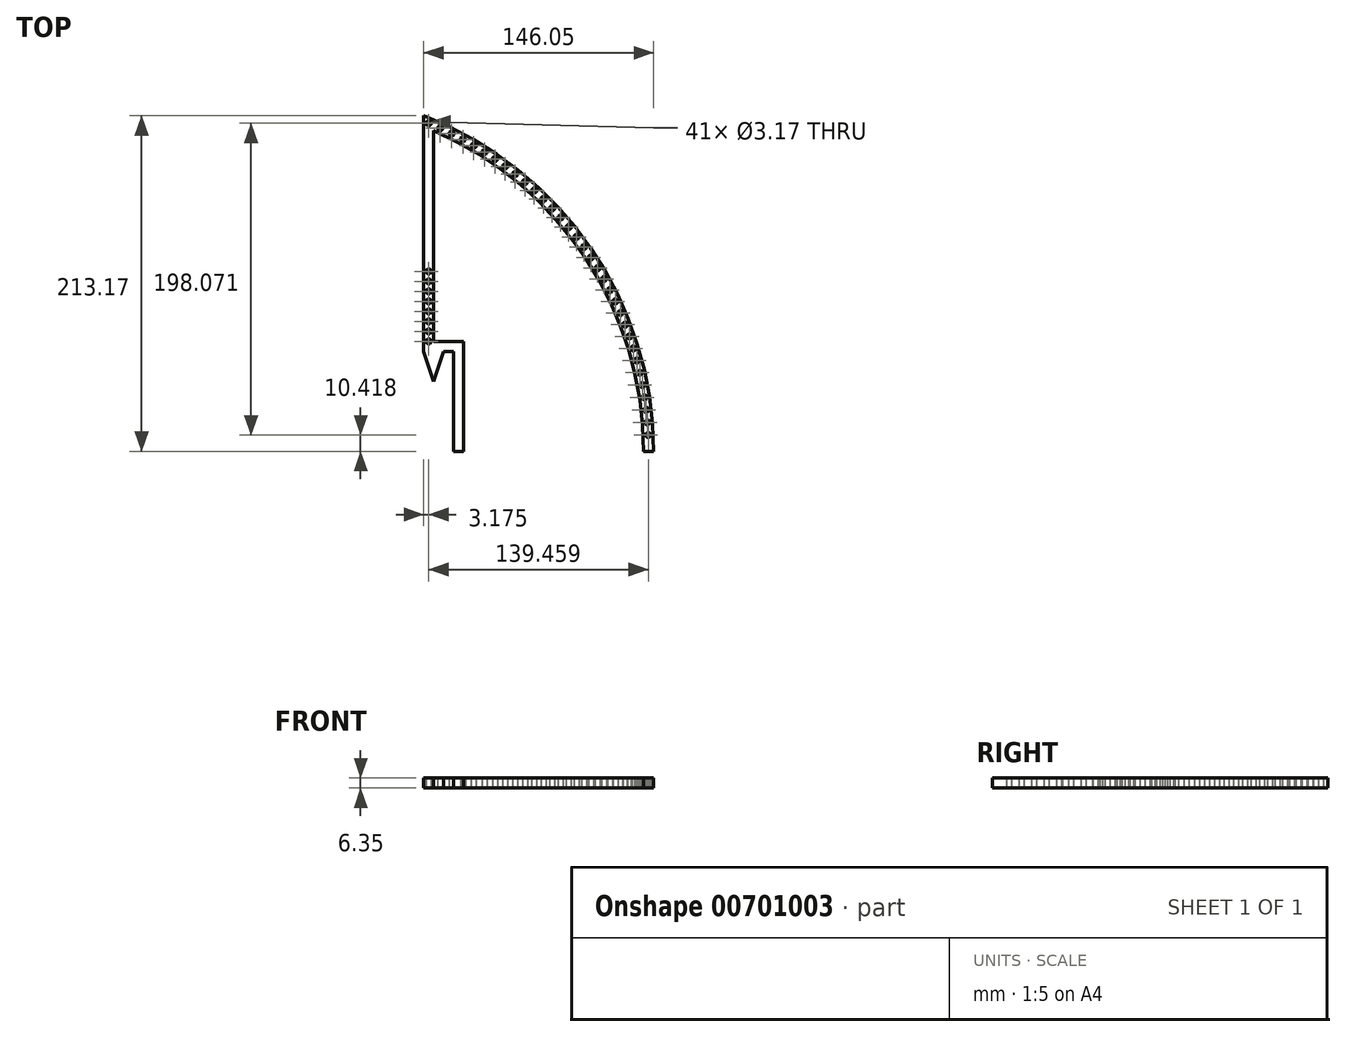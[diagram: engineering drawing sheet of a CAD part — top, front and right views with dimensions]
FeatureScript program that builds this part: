
annotation { "Feature Type Name" : "Feature", "Feature Type Description" : "" }
export const myFeature = defineFeature(function(context is Context, id is Id, definition is map)
    precondition{}
    {
        {
            var Q0;
            Q0=qCreatedBy(makeId("Top.planeOp"),FACE);
            var sketch = newSketch(context, id + "F0", { "sketchPlane" : qUnion([Q0])});
            skLineSegment(sketch, "E0", {"start": v(0, 0) * mm, "end": v(-82.55, 0) * mm, "construction": true});
            skCircle(sketch, "E1", {"center": v(-82.55, 0) * mm, "radius": 254 * mm, "construction": true});
            skLineSegment(sketch, "E2", {"start": v(0, 0) * mm, "end": v(0, 63.5) * mm, "construction": true});
            skLineSegment(sketch, "E3", {"start": v(0, 0) * mm, "end": v(19.05, 0) * mm, "construction": true});
            skLineSegment(sketch, "E4", {"start": v(19.05, 0) * mm, "end": v(19.05, 63.5) * mm});
            skLineSegment(sketch, "E5", {"start": v(19.05, 63.5) * mm, "end": v(12.7, 63.5) * mm});
            skLineSegment(sketch, "E6", {"start": v(0, 63.5) * mm, "end": v(12.7, 63.5) * mm, "construction": true});
            skLineSegment(sketch, "E7", {"start": v(6.35, 63.5) * mm, "end": v(6.35, 44.45) * mm, "construction": true});
            skLineSegment(sketch, "E8", {"start": v(0, 63.5) * mm, "end": v(6.35, 44.45) * mm});
            skLineSegment(sketch, "E9", {"start": v(12.7, 63.5) * mm, "end": v(6.35, 44.45) * mm});
            skCircle(sketch, "E10", {"center": v(-82.55, 0) * mm, "radius": 228.6 * mm, "construction": true});
            skLineSegment(sketch, "E11", {"start": v(0, 63.5) * mm, "end": v(0, 213.17) * mm});
            skArc(sketch, "E12", {"start": v(0, 213.17) * mm, "mid": v(106.04, 129.2) * mm, "end": v(146.05, 0) * mm});
            skArc(sketch, "E13.0", {"start": v(6.35, 203.7) * mm, "mid": v(103.4, 121.73) * mm, "end": v(139.7, 0) * mm});
            skLineSegment(sketch, "E13.1", {"start": v(25.4, 0) * mm, "end": v(25.4, 69.85) * mm});
            skLineSegment(sketch, "E13.2", {"start": v(25.4, 69.85) * mm, "end": v(12.7, 69.85) * mm});
            skLineSegment(sketch, "E13.3", {"start": v(6.35, 69.85) * mm, "end": v(12.7, 69.85) * mm});
            skLineSegment(sketch, "E13.4", {"start": v(6.35, 69.85) * mm, "end": v(6.35, 203.7) * mm});
            skLineSegment(sketch, "E14", {"start": v(19.05, 0) * mm, "end": v(25.4, 0) * mm});
            skLineSegment(sketch, "E15", {"start": v(139.7, 0) * mm, "end": v(146.05, 0) * mm});
            skLineSegment(sketch, "E16", {"start": v(6.35, 203.7) * mm, "end": v(0, 203.7) * mm, "construction": true});
            skLineSegment(sketch, "E17", {"start": v(3.17, 203.7) * mm, "end": v(3.17, 69.85) * mm, "construction": true});
            skCircle(sketch, "E18", {"center": v(3.17, 69.85) * mm, "radius": 1.59 * mm});
            skCircle(sketch, "E19.0.1.0", {"center": v(3.17, 76.2) * mm, "radius": 1.59 * mm});
            skCircle(sketch, "E19.0.2.0", {"center": v(3.17, 82.55) * mm, "radius": 1.59 * mm});
            skCircle(sketch, "E19.0.3.0", {"center": v(3.17, 88.9) * mm, "radius": 1.59 * mm});
            skCircle(sketch, "E19.0.4.0", {"center": v(3.17, 95.25) * mm, "radius": 1.59 * mm});
            skCircle(sketch, "E19.0.5.0", {"center": v(3.17, 101.6) * mm, "radius": 1.59 * mm});
            skLineSegment(sketch, "E19.direction1", {"start": v(3.17, 69.85) * mm, "end": v(28.57, 69.85) * mm, "construction": true});
            skLineSegment(sketch, "E19.direction2", {"start": v(3.17, 69.85) * mm, "end": v(3.17, 76.2) * mm, "construction": true});
            skCircle(sketch, "E20.0.0.6", {"center": v(3.17, 107.95) * mm, "radius": 1.59 * mm});
            skCircle(sketch, "E20.0.0.7", {"center": v(3.17, 114.3) * mm, "radius": 1.59 * mm});
            skCircle(sketch, "E21", {"center": v(-82.55, 0) * mm, "radius": 225.43 * mm, "construction": true});
            skCircle(sketch, "E22", {"center": v(3.17, 208.49) * mm, "radius": 1.59 * mm});
            skCircle(sketch, "E23.1.0", {"center": v(10.51, 205.32) * mm, "radius": 1.59 * mm});
            skCircle(sketch, "E23.2.0", {"center": v(17.73, 201.9) * mm, "radius": 1.59 * mm});
            skCircle(sketch, "E23.3.0", {"center": v(24.82, 198.21) * mm, "radius": 1.59 * mm});
            skCircle(sketch, "E23.4.0", {"center": v(31.78, 194.28) * mm, "radius": 1.59 * mm});
            skCircle(sketch, "E23.5.0", {"center": v(38.6, 190.1) * mm, "radius": 1.59 * mm});
            skCircle(sketch, "E23.6.0", {"center": v(45.26, 185.7) * mm, "radius": 1.59 * mm});
            skCircle(sketch, "E23.7.0", {"center": v(51.76, 181.05) * mm, "radius": 1.59 * mm});
            skCircle(sketch, "E23.8.0", {"center": v(58.1, 176.17) * mm, "radius": 1.59 * mm});
            skCircle(sketch, "E23.9.0", {"center": v(64.25, 171.08) * mm, "radius": 1.59 * mm});
            skCircle(sketch, "E23.10.0", {"center": v(70.22, 165.77) * mm, "radius": 1.59 * mm});
            skCircle(sketch, "E23.11.0", {"center": v(76, 160.25) * mm, "radius": 1.59 * mm});
            skCircle(sketch, "E23.12.0", {"center": v(81.58, 154.53) * mm, "radius": 1.59 * mm});
            skCircle(sketch, "E23.13.0", {"center": v(86.95, 148.61) * mm, "radius": 1.59 * mm});
            skCircle(sketch, "E23.14.0", {"center": v(92.11, 142.5) * mm, "radius": 1.59 * mm});
            skCircle(sketch, "E23.15.0", {"center": v(97.06, 136.23) * mm, "radius": 1.59 * mm});
            skCircle(sketch, "E23.16.0", {"center": v(101.77, 129.78) * mm, "radius": 1.59 * mm});
            skCircle(sketch, "E23.17.0", {"center": v(106.25, 123.16) * mm, "radius": 1.59 * mm});
            skCircle(sketch, "E23.18.0", {"center": v(110.5, 116.4) * mm, "radius": 1.59 * mm});
            skCircle(sketch, "E23.19.0", {"center": v(114.5, 109.48) * mm, "radius": 1.59 * mm});
            skCircle(sketch, "E23.20.0", {"center": v(118.26, 102.42) * mm, "radius": 1.59 * mm});
            skCircle(sketch, "E23.21.0", {"center": v(121.77, 95.24) * mm, "radius": 1.59 * mm});
            skCircle(sketch, "E23.22.0", {"center": v(125.01, 87.94) * mm, "radius": 1.59 * mm});
            skCircle(sketch, "E23.23.0", {"center": v(128, 80.53) * mm, "radius": 1.59 * mm});
            skCircle(sketch, "E23.24.0", {"center": v(130.72, 73.01) * mm, "radius": 1.59 * mm});
            skCircle(sketch, "E23.25.0", {"center": v(133.18, 65.4) * mm, "radius": 1.59 * mm});
            skCircle(sketch, "E23.26.0", {"center": v(135.36, 57.72) * mm, "radius": 1.59 * mm});
            skCircle(sketch, "E23.27.0", {"center": v(137.27, 49.96) * mm, "radius": 1.59 * mm});
            skCircle(sketch, "E23.28.0", {"center": v(138.9, 42.14) * mm, "radius": 1.59 * mm});
            skCircle(sketch, "E23.29.0", {"center": v(140.26, 34.26) * mm, "radius": 1.59 * mm});
            skCircle(sketch, "E23.30.0", {"center": v(141.33, 26.34) * mm, "radius": 1.59 * mm});
            skCircle(sketch, "E23.31.0", {"center": v(142.12, 18.4) * mm, "radius": 1.59 * mm});
            skCircle(sketch, "E23.32.0", {"center": v(142.63, 10.42) * mm, "radius": 1.59 * mm});
            skLineSegment(sketch, "E23.anchor1", {"start": v(-82.55, 0) * mm, "end": v(3.17, 208.49) * mm, "construction": true});
            skLineSegment(sketch, "E23.anchor2", {"start": v(-82.55, 0) * mm, "end": v(142.63, 10.42) * mm, "construction": true});
            skLineSegment(sketch, "E24", {"start": v(0, 213.17) * mm, "end": v(-165.1, 213.17) * mm, "construction": true});
            skArc(sketch, "E25", {"start": v(-165.1, 213.17) * mm, "mid": v(-82.55, 228.6) * mm, "end": v(0, 213.17) * mm});
            skLineSegment(sketch, "E26", {"start": v(-165.1, 213.17) * mm, "end": v(-165.1, 175.07) * mm});
            skLineSegment(sketch, "E27", {"start": v(-165.1, 175.07) * mm, "end": v(0, 175.07) * mm});
            skLineSegment(sketch, "E28", {"start": v(-82.55, 175.07) * mm, "end": v(-82.55, 228.6) * mm, "construction": true});
            skLineSegment(sketch, "E29", {"start": v(-82.55, 175.07) * mm, "end": v(-82.55, 181.42) * mm, "construction": true});
            skSolve(sketch);
        }
        {
            var Q0;
            Q0=makeQuery(id+"F0.imprint","IMPRINT",FACE,{"disambiguationData":[TD([[makeQuery(id+"F0.imprint","IMPRINT",EDGE,{"derivedFrom":sQuery(id+"F0.wireOp",EDGE,"E4")}),-1.0]])]});
            extrude(context, id + "F1", {"entities" : qUnion([Q0]), "depth" : 6.35 * mm, "offsetDistance" : 25.4 * mm});
        }
    });
